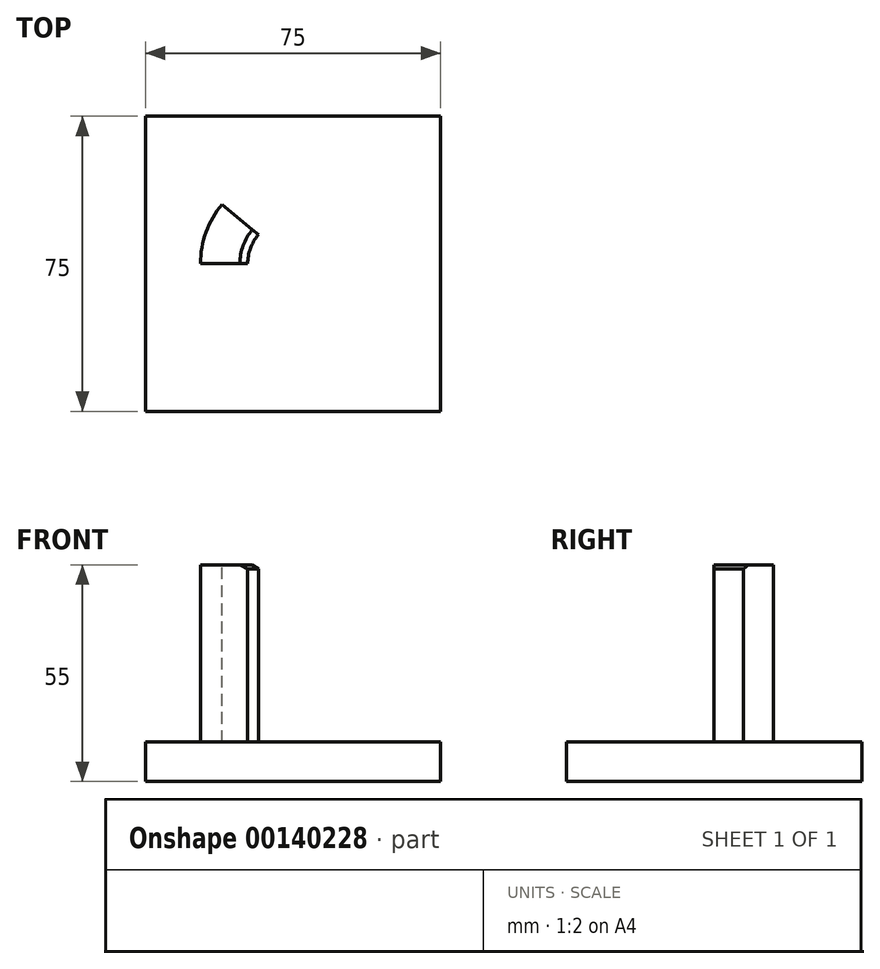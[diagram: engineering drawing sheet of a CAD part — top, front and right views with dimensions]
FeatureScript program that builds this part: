
annotation { "Feature Type Name" : "Feature", "Feature Type Description" : "" }
export const myFeature = defineFeature(function(context is Context, id is Id, definition is map)
    precondition{}
    {
        {
            var Q0;
            Q0=qCreatedBy(makeId("Top.planeOp"),FACE);
            var sketch = newSketch(context, id + "F0", { "sketchPlane" : qUnion([Q0])});
            skLineSegment(sketch, "E0", {"start": v(0, 65.15) * mm, "end": v(0, -74.15) * mm, "construction": true});
            skLineSegment(sketch, "E1", {"start": v(-73.04, 0) * mm, "end": v(85.28, 0) * mm, "construction": true});
            skLineSegment(sketch, "E2.bottom", {"start": v(37.5, 37.5) * mm, "end": v(-37.5, 37.5) * mm});
            skLineSegment(sketch, "E2.top", {"start": v(37.5, -37.5) * mm, "end": v(-37.5, -37.5) * mm});
            skLineSegment(sketch, "E2.left", {"start": v(37.5, 37.5) * mm, "end": v(37.5, -37.5) * mm});
            skLineSegment(sketch, "E2.right", {"start": v(-37.5, 37.5) * mm, "end": v(-37.5, -37.5) * mm});
            skPoint(sketch, "E2.middle", {"position": v(0, 0) * mm});
            skSolve(sketch);
        }
        {
            var Q0;
            Q0=qSketchRegion(id+"F0",true);
            extrude(context, id + "F1", {"entities" : qUnion([Q0]), "depth" : 10 * mm});
        }
        {
            var Q0;
            Q0=qCreatedBy(makeId("Front.planeOp"),FACE);
            var sketch = newSketch(context, id + "F2", { "sketchPlane" : qUnion([Q0])});
            skLineSegment(sketch, "E3", {"start": v(-46.02, 0) * mm, "end": v(46.67, 0) * mm, "construction": true});
            skLineSegment(sketch, "E4", {"start": v(0, 74.4) * mm, "end": v(0, -5.6) * mm, "construction": true});
            skLineSegment(sketch, "E5.top", {"start": v(-23.5, 55) * mm, "end": v(-13.5, 55) * mm});
            skLineSegment(sketch, "E5.left", {"start": v(-23.5, 10) * mm, "end": v(-23.5, 55) * mm});
            skLineSegment(sketch, "E5.right", {"start": v(-13.5, 10) * mm, "end": v(-13.5, 55) * mm});
            skLineSegment(sketch, "E6", {"start": v(-13.5, 55) * mm, "end": v(-11.5, 53.94) * mm});
            skLineSegment(sketch, "E7", {"start": v(-11.5, 53.94) * mm, "end": v(-11.5, 10) * mm});
            skLineSegment(sketch, "E8", {"start": v(-11.5, 10) * mm, "end": v(-13.5, 10) * mm});
            skLineSegment(sketch, "E9", {"start": v(-11.5, 53.94) * mm, "end": v(-13.5, 53.94) * mm, "construction": true});
            skLineSegment(sketch, "E10", {"start": v(-23.5, 10) * mm, "end": v(-13.5, 10) * mm});
            skSolve(sketch);
        }
        {
            var Q0;
            Q0=qSketchRegion(id+"F2",true);
            var Q1;
            Q1=sQuery(id+"F2.wireOp",EDGE,"E4");
            revolve(context, id + "F3", {"operationType" : NewBodyOperationType.ADD, "entities" : qUnion([Q0]), "axis" : qUnion([Q1]), "revolveType" : RevolveType.ONE_DIRECTION, "angle" : 40 * degree});
        }
    });
